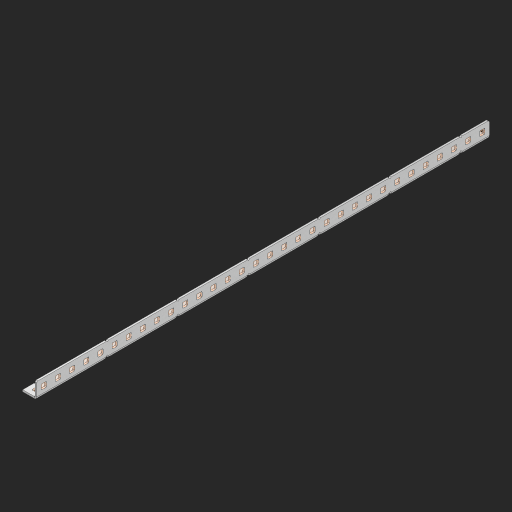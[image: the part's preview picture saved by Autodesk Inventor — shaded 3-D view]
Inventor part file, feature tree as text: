
AUTODESK INVENTOR PART (.ipt)
format: ipt  version: 2023 (Build 270158000, 158)  size: 1,307,648 bytes
history: native  units: in
note: dims shown in document units (in); Inventor stores cm internally (conversion verified against a paired STEP export)
features: other x244, extrude x94, sheet_metal_op x11, sketch x10, pattern_linear x2, mirror x1, chamfer x1
ambient origin geometry x8: Origin, YZ Plane, XZ Plane, XY Plane, X Axis, Y Axis, Z Axis, Center Point
bodies: Solid1 (feature_tree), Body (feature_tree)
feature tree (363):
  other  "Alu Half C 1x2x1x32"
  other  "Table"
  other  "Alu C 1x2x1x35"
  other  "Alu C 1x2x1x34"
  other  "Alu C 1x2x1x33"
  other  "Alu C 1x2x1x32"
  other  "Alu C 1x2x1x31"
  other  "Alu C 1x2x1x30"
  other  "Alu C 1x2x1x29"
  other  "Alu C 1x2x1x28"
  other  "Alu C 1x2x1x27"
  other  "Alu C 1x2x1x26"
  other  "Alu C 1x2x1x25"
  other  "Alu C 1x2x1x24"
  other  "Alu C 1x2x1x23"
  other  "Alu C 1x2x1x22"
  other  "Alu C 1x2x1x21"
  other  "Alu C 1x2x1x20"
  other  "Alu C 1x2x1x19"
  other  "Alu C 1x2x1x18"
  other  "Alu C 1x2x1x17"
  other  "Alu C 1x2x1x16"
  other  "Alu C 1x2x1x15"
  other  "Alu C 1x2x1x14"
  other  "Alu C 1x2x1x13"
  other  "Alu C 1x2x1x12"
  other  "Alu C 1x2x1x11"
  other  "Alu C 1x2x1x10"
  other  "Alu C 1x2x1x9"
  other  "Alu C 1x2x1x8"
  other  "Alu C 1x2x1x7"
  other  "Alu C 1x2x1x6"
  other  "Alu C 1x2x1x5"
  other  "Alu C 1x2x1x4"
  other  "Alu C 1x2x1x3"
  other  "Alu C 1x2x1x2"
  other  "Alu C 1x2x1x1"
  other  "Steel C 1x2x1x35"
  other  "Steel C 1x2x1x34"
  other  "Steel C 1x2x1x33"
  other  "Steel C 1x2x1x32"
  other  "Steel C 1x2x1x31"
  other  "Steel C 1x2x1x30"
  other  "Steel C 1x2x1x29"
  other  "Steel C 1x2x1x28"
  other  "Steel C 1x2x1x27"
  other  "Steel C 1x2x1x26"
  other  "Steel C 1x2x1x25"
  other  "Steel C 1x2x1x24"
  other  "Steel C 1x2x1x23"
  other  "Steel C 1x2x1x22"
  other  "Steel C 1x2x1x21"
  other  "Steel C 1x2x1x20"
  other  "Steel C 1x2x1x19"
  other  "Steel C 1x2x1x18"
  other  "Steel C 1x2x1x17"
  other  "Steel C 1x2x1x16"
  other  "Steel C 1x2x1x15"
  other  "Steel C 1x2x1x14"
  other  "Steel C 1x2x1x13"
  other  "Steel C 1x2x1x12"
  other  "Steel C 1x2x1x11"
  other  "Steel C 1x2x1x10"
  other  "Steel C 1x2x1x9"
  other  "Steel C 1x2x1x8"
  other  "Steel C 1x2x1x7"
  other  "Steel C 1x2x1x6"
  other  "Steel C 1x2x1x5"
  other  "Steel C 1x2x1x4"
  other  "Steel C 1x2x1x3"
  other  "Steel C 1x2x1x2"
  other  "Steel C 1x2x1x1"
  other  "Alu Half C 1x2x1x35"
  other  "Alu Half C 1x2x1x34"
  other  "Alu Half C 1x2x1x33"
  other  "Alu Half C 1x2x1x31"
  other  "Alu Half C 1x2x1x30"
  other  "Alu Half C 1x2x1x29"
  other  "Alu Half C 1x2x1x28"
  other  "Alu Half C 1x2x1x27"
  other  "Alu Half C 1x2x1x26"
  other  "Alu Half C 1x2x1x25"
  other  "Alu Half C 1x2x1x24"
  other  "Alu Half C 1x2x1x23"
  other  "Alu Half C 1x2x1x22"
  other  "Alu Half C 1x2x1x21"
  other  "Alu Half C 1x2x1x20"
  other  "Alu Half C 1x2x1x19"
  other  "Alu Half C 1x2x1x18"
  other  "Alu Half C 1x2x1x17"
  other  "Alu Half C 1x2x1x16"
  other  "Alu Half C 1x2x1x15"
  other  "Alu Half C 1x2x1x14"
  other  "Alu Half C 1x2x1x13"
  other  "Alu Half C 1x2x1x12"
  other  "Alu Half C 1x2x1x11"
  other  "Alu Half C 1x2x1x10"
  other  "Alu Half C 1x2x1x9"
  other  "Alu Half C 1x2x1x8"
  other  "Alu Half C 1x2x1x7"
  other  "Alu Half C 1x2x1x6"
  other  "Alu Half C 1x2x1x5"
  other  "Alu Half C 1x2x1x4"
  other  "Alu Half C 1x2x1x3"
  other  "Alu Half C 1x2x1x2"
  other  "Alu Half C 1x2x1x1"
  other  "Steel Half C 1x2x1x35"
  other  "Steel Half C 1x2x1x34"
  other  "Steel Half C 1x2x1x33"
  other  "Steel Half C 1x2x1x32"
  other  "Steel Half C 1x2x1x31"
  other  "Steel Half C 1x2x1x30"
  other  "Steel Half C 1x2x1x29"
  other  "Steel Half C 1x2x1x28"
  other  "Steel Half C 1x2x1x27"
  other  "Steel Half C 1x2x1x26"
  other  "Steel Half C 1x2x1x25"
  other  "Steel Half C 1x2x1x24"
  other  "Steel Half C 1x2x1x23"
  other  "Steel Half C 1x2x1x22"
  other  "Steel Half C 1x2x1x21"
  other  "Steel Half C 1x2x1x20"
  other  "Steel Half C 1x2x1x19"
  other  "Steel Half C 1x2x1x18"
  other  "Steel Half C 1x2x1x17"
  other  "Steel Half C 1x2x1x16"
  other  "Steel Half C 1x2x1x15"
  other  "Steel Half C 1x2x1x14"
  other  "Steel Half C 1x2x1x13"
  other  "Steel Half C 1x2x1x12"
  other  "Steel Half C 1x2x1x11"
  other  "Steel Half C 1x2x1x10"
  other  "Steel Half C 1x2x1x9"
  other  "Steel Half C 1x2x1x8"
  other  "Steel Half C 1x2x1x7"
  other  "Steel Half C 1x2x1x6"
  other  "Steel Half C 1x2x1x5"
  other  "Steel Half C 1x2x1x4"
  other  "Steel Half C 1x2x1x3"
  other  "Steel Half C 1x2x1x2"
  other  "Steel Half C 1x2x1x1"
  sheet_metal_op  "Flanges"
  other  "Flange Pattern Plane"
  other  "Flange Pattern Sketch"
  sheet_metal_op  "Flange Pattern"
  sheet_metal_op  "Body Pattern"
  pattern_linear  "Center Pattern"  Spacing1=0.0625in  [1 undecoded]
  other  "Arc Length"
  mirror  "Notch Mirror"
  pattern_linear  "Notch Pattern"  Spacing1=0.182in  [1 undecoded]
  chamfer  "End Chamfer"
  extrude  "Half Cut"  Depth=0.02in
  sketch  "Sketch1"  dims[d0=1.0in]
  other  "Plate1"
  sketch  "Sketch2"  dims[d1=16.0in]
  other  "Plate2"
  sheet_metal_op  "Bend1"
  sheet_metal_op  "Corner1"
  sketch  "Sketch3"  dims[d2=0.0625in]
  sketch  "Sketch7"  dims[d3=0.0625in]
  other  "Srf1"
  other  "Srf2"
  sketch  "Sketch8"  dims[d4=0.0312in]
  sketch  "Sketch9"  dims[d5=0.125in]
  other  "Srf91"
  sheet_metal_op  "Body Pattern Sketch"
  other  "Srf92"
  sketch  "Sketch13"  dims[d6=0.0625in]
  sketch  "Sketch14"  dims[d7=0.5in d8=90.0deg d9=0.0312in]
  sketch  "Sketch15"  dims[d10=0.25in]
  sketch  "Sketch16"  dims[d11=0.0625in d12=0.0625in d16=0.182in d17=0.02in d18=0.0625in d19=0.0in d20=0.25in d21=0.25in d38=12.5984in d40=0.5in d41=0.3937in d43=1.0in d46=0.172in d47=1.0in d48=0.0in d49=0.182in d50=0.02in d51=0.25in d52=0.25in d53=0.0625in d54=0.0in d55=0.172in d56=1.0in d57=0.0in d58=0.25in d60=12.5984in d62=0.5in d63=0.3937in d65=0.5in d85=0.1473in d86=0.1782in d88=0.04in d89=0.0625in d90=0.0in d91=0.04in d92=0.0491in d95=2.5in d96=0.04in d97=0.25in d98=45.0deg d99=0.25in d100=0.5in d101=0.0in d102=2.497in d106=0.182in d107=0.02in d108=0.5in d109=0.5in d110=0.0625in d111=0.0in d112=0.172in d113=0.5in d114=0.0in d117=0.5in d118=0.5in d119=0.5in]
  other  "Srf786"
  other  "Srf823"
  other  "Srf824"
  other  "Srf825"
  other  "Srf826"
  other  "Srf827"
  other  "Srf828"
  other  "Srf829"
  other  "Srf856"
  other  "Srf857"
  other  "Srf858"
  other  "Srf859"
  other  "Srf860"
  other  "Srf861"
  other  "Srf862"
  other  "Srf889"
  other  "Srf890"
  other  "Srf891"
  other  "Srf892"
  other  "Srf893"
  other  "Srf894"
  other  "Srf895"
  other  "Srf896"
  other  "Srf922"
  other  "Srf923"
  other  "Srf924"
  other  "Srf925"
  other  "Srf926"
  other  "Srf959"
  other  "Srf960"
  other  "Srf961"
  other  "Srf962"
  other  "Srf963"
  other  "Srf996"
  other  "Srf997"
  other  "Srf998"
  other  "Srf999"
  other  "Srf1000"
  other  "Srf1143"
  other  "Srf1144"
  other  "Srf1145"
  other  "Srf1146"
  other  "Srf1147"
  other  "Srf1148"
  other  "Srf1149"
  other  "Srf1150"
  other  "Srf1151"
  other  "Srf1152"
  other  "Srf1153"
  other  "Srf1154"
  other  "Srf1155"
  other  "Srf1156"
  other  "Srf1157"
  other  "Srf1158"
  other  "Srf1159"
  other  "Srf1160"
  other  "Srf1199"
  other  "Srf1200"
  other  "Srf1201"
  other  "Srf1202"
  other  "Srf1203"
  other  "Srf1204"
  other  "Srf1205"
  other  "Srf1206"
  other  "Srf1207"
  other  "Srf1208"
  other  "Srf1209"
  other  "Srf1210"
  other  "Srf1211"
  other  "Srf1212"
  other  "Srf1213"
  other  "Srf1214"
  other  "Srf1215"
  other  "Srf1216"
  other  "Srf1255"
  other  "Srf1256"
  other  "Srf1257"
  other  "Srf1258"
  other  "Srf1259"
  other  "Srf1260"
  other  "Srf1261"
  other  "Srf1262"
  other  "Srf1263"
  other  "Srf1264"
  other  "Srf1265"
  other  "Srf1266"
  other  "Srf1267"
  other  "Srf1268"
  other  "Srf1269"
  other  "Srf1270"
  other  "Srf1271"
  other  "Srf1272"
  sheet_metal_op  "Flange Stamp"
  sheet_metal_op  "Flange Circle"
  sheet_metal_op  "Body Stamp"
  sheet_metal_op  "Body Circle"
  other  "Center Stamp"
  other  "Center Circle"
  sheet_metal_op  "Notch"
  extrude  "ExtrusionSrf2"  Depth=0.0625in
  extrude  "ExtrusionSrf92"  TaperAngle=0.0deg  [1 undecoded]
  extrude  "ExtrusionSrf823"  Depth=0.25in
  extrude  "ExtrusionSrf824"  Depth=0.25in
  extrude  "ExtrusionSrf825"  Depth=0.5in
  extrude  "ExtrusionSrf826"  Depth=0.5in
  extrude  "ExtrusionSrf827"  Depth=1.0in TaperAngle=0.0deg
  extrude  "ExtrusionSrf828"  Depth=0.182in
  extrude  "ExtrusionSrf829"  Depth=0.02in
  extrude  "ExtrusionSrf856"  Depth=0.25in
  extrude  "ExtrusionSrf857"  Depth=0.25in
  extrude  "ExtrusionSrf858"  Depth=0.0625in
  extrude  "ExtrusionSrf859"  TaperAngle=0.0deg  [1 undecoded]
  extrude  "ExtrusionSrf860"  Depth=0.5in
  extrude  "ExtrusionSrf861"  Depth=1.0in TaperAngle=0.0deg
  extrude  "ExtrusionSrf862"  Depth=0.25in
  extrude  "ExtrusionSrf889"  Depth=0.5in
  extrude  "ExtrusionSrf890"  Depth=0.5in
  extrude  "ExtrusionSrf891"  Depth=0.5in
  extrude  "ExtrusionSrf892"  Depth=0.5in
  extrude  "ExtrusionSrf893"  Depth=0.5in
  extrude  "ExtrusionSrf894"  Depth=0.0625in
  extrude  "ExtrusionSrf895"  TaperAngle=0.0deg  [1 undecoded]
  extrude  "ExtrusionSrf896"  Depth=0.5in
  extrude  "ExtrusionSrf922"  Depth=0.5in
  extrude  "ExtrusionSrf923"  Depth=2.5in
  extrude  "ExtrusionSrf924"  Depth=0.25in TaperAngle=45.0deg
  extrude  "ExtrusionSrf925"  Depth=0.25in
  extrude  "ExtrusionSrf926"  Depth=0.5in TaperAngle=0.0deg
  extrude  "ExtrusionSrf959"  Depth=0.5in
  extrude  "ExtrusionSrf960"  Depth=0.182in
  extrude  "ExtrusionSrf961"  Depth=0.02in
  extrude  "ExtrusionSrf962"  Depth=0.5in
  extrude  "ExtrusionSrf963"  Depth=0.5in
  extrude  "ExtrusionSrf996"  Depth=0.0625in
  extrude  "ExtrusionSrf997"  TaperAngle=0.0deg  [1 undecoded]
  extrude  "ExtrusionSrf998"  Depth=0.5in
  extrude  "ExtrusionSrf999"  Depth=0.5in TaperAngle=0.0deg
  extrude  "ExtrusionSrf1000"  Depth=0.5in
  extrude  "ExtrusionSrf1143"  Depth=0.5in
  extrude  "ExtrusionSrf1144"  Depth=0.5in
  extrude  "ExtrusionSrf1145"  [1 undecoded]
  extrude  "ExtrusionSrf1146"  [1 undecoded]
  extrude  "ExtrusionSrf1147"  [1 undecoded]
  extrude  "ExtrusionSrf1148"  [1 undecoded]
  extrude  "ExtrusionSrf1149"  [1 undecoded]
  extrude  "ExtrusionSrf1150"  [1 undecoded]
  extrude  "ExtrusionSrf1151"  [1 undecoded]
  extrude  "ExtrusionSrf1152"  [1 undecoded]
  extrude  "ExtrusionSrf1153"  [1 undecoded]
  extrude  "ExtrusionSrf1154"  [1 undecoded]
  extrude  "ExtrusionSrf1155"  [1 undecoded]
  extrude  "ExtrusionSrf1156"  [1 undecoded]
  extrude  "ExtrusionSrf1157"  [1 undecoded]
  extrude  "ExtrusionSrf1158"  [1 undecoded]
  extrude  "ExtrusionSrf1159"  [1 undecoded]
  extrude  "ExtrusionSrf1160"  [1 undecoded]
  extrude  "ExtrusionSrf1199"  [1 undecoded]
  extrude  "ExtrusionSrf1200"  [1 undecoded]
  extrude  "ExtrusionSrf1201"  [1 undecoded]
  extrude  "ExtrusionSrf1202"  [1 undecoded]
  extrude  "ExtrusionSrf1203"  [1 undecoded]
  extrude  "ExtrusionSrf1204"  [1 undecoded]
  extrude  "ExtrusionSrf1205"  [1 undecoded]
  extrude  "ExtrusionSrf1206"  [1 undecoded]
  extrude  "ExtrusionSrf1207"  [1 undecoded]
  extrude  "ExtrusionSrf1208"  [1 undecoded]
  extrude  "ExtrusionSrf1209"  [1 undecoded]
  extrude  "ExtrusionSrf1210"  [1 undecoded]
  extrude  "ExtrusionSrf1211"  [1 undecoded]
  extrude  "ExtrusionSrf1212"  [1 undecoded]
  extrude  "ExtrusionSrf1213"  [1 undecoded]
  extrude  "ExtrusionSrf1214"  [1 undecoded]
  extrude  "ExtrusionSrf1215"  [1 undecoded]
  extrude  "ExtrusionSrf1216"  [1 undecoded]
  extrude  "ExtrusionSrf1255"  [1 undecoded]
  extrude  "ExtrusionSrf1256"  [1 undecoded]
  extrude  "ExtrusionSrf1257"  [1 undecoded]
  extrude  "ExtrusionSrf1258"  [1 undecoded]
  extrude  "ExtrusionSrf1259"  [1 undecoded]
  extrude  "ExtrusionSrf1260"  [1 undecoded]
  extrude  "ExtrusionSrf1261"  [1 undecoded]
  extrude  "ExtrusionSrf1262"  [1 undecoded]
  extrude  "ExtrusionSrf1263"  [1 undecoded]
  extrude  "ExtrusionSrf1264"  [1 undecoded]
  extrude  "ExtrusionSrf1265"  [1 undecoded]
  extrude  "ExtrusionSrf1266"  [1 undecoded]
  extrude  "ExtrusionSrf1267"  [1 undecoded]
  extrude  "ExtrusionSrf1268"  [1 undecoded]
  extrude  "ExtrusionSrf1269"  [1 undecoded]
  extrude  "ExtrusionSrf1270"  [1 undecoded]
  extrude  "ExtrusionSrf1271"  [1 undecoded]
  extrude  "ExtrusionSrf1272"  [1 undecoded]
note: 58 required parameter values undecoded (feature->parameter linkage not recoverable at this tier; creation-order binding heuristic only, values carry confidence <= 0.55)
